# Revit family: R-MBF-271
name_source: partatom
category: Portes
units: mm (PartAtom-declared; Revit-internal decimal feet)

## family parameters
Couper avec des vides une fois chargée = Non
Hôte = Mur
Partagée = Non
Point de calcul de pièce = Oui
Toujours verticalement = Oui

## types (1)
- MBF-271
    1 Vantail = Oui
    2 Vantaux = Non
    A.E.V = non
    Acoustique = non
    Anti-Effraction = non
    Code_MAJ = 2303130305MBF271
    Coloris_Chants = BER
    Coloris_Dormant = Hêtre
    Coloris_Face_Cote_Oppose_Ouverture = Prépeint
    Coloris_Face_Cote_Ouverture = Prépeint
    Construction analytique = <Aucun>
    DAS = Non
    DC Larg Feuillure = 12 mm  [stored 0.0393701 ft]
    DC Pivot Vantail = 60 mm  [stored 0.19685 ft]
    Description = Bloc-porte bois RESISTANT AU FEU 1 vantail grandes dimensions avec pivot linteau encastré et joint anti-pince doigt côté battement, double action / va-et-vient, EI30, sur huisserie bois
    Ep Profil Pose Tunnel = 118 mm
    Ep Strat Vantail = 1 mm  [stored 0.00328084 ft]
    Ep Vantail = 46 mm  [stored 0.150919 ft]
    Epaisseur_Rainure à brique = 8 mm  [stored 0.0262467 ft]
    FDES Inies = https://www.base-inies.fr
https://www.base-inies.fr
    Fabricant = MALERBA
    Fiche_Produit = MBF-271
    Fileur = Non
    Hauteur_Tableau = 2120 mm  [stored 6.95538 ft]
    Hauteur_Vantaux_Souhaitée = 2040 mm  [stored 6.69291 ft]
    Jeu_1 = 0 mm  [stored 0 ft]
    Jeu_2 = 0 mm  [stored 0 ft]
    Jeu_Côté_Articulation_Vantail = 8 mm  [stored 0.0262467 ft]
    Jeu_Côté_Fermeture_Vantail = 8 mm  [stored 0.0262467 ft]
    Jeu_Haut = 3 mm  [stored 0.00984252 ft]
    Larg Profil = 58 mm  [stored 0.190289 ft]
    Larg Profil Avec Fileur = 20 mm  [stored 0.0656168 ft]
    Larg Profil Trav = 76 mm  [stored 0.249344 ft]
    Largeur = 0 mm  [stored 0 ft]
    Largeur_Vantail_Semi_Fixe_Souhaitée = 630 mm  [stored 2.06693 ft]
    Largeur_Vantail_Service_Souhaitée = 930 mm  [stored 3.05118 ft]
    Mat APD = Caoutchouc noir
    Mat Parclose = BER 2
    Mat Parclose Métal = Peinture Laquée PMT - Blanc Pur - RAL 9010
    Materiaux_Dominant = Bois
    Modèle = Va et vient
    Montant_VV = Oui
    Note d'identification = 1V EI30 - GD - LINTEAU (APD MD) - HUISSERIE BOIS
    Profondeur_Rainure à brique = 5 mm  [stored 0.0164042 ft]
    Reference_Commerciale = 1V/DA GD LINTEAU
    Resistance_Feu = EI30
    Sans_Montants = Non
    Sens_Feu = Recto / Verso
    Thermique (W/m2.°K) = 0
    URL = https://www.malerba.fr
    X_Axe Pivot = 114 mm  [stored 0.374016 ft]
    X_DC seuil = 9 mm  [stored 0.0295276 ft]
    X_Inv_DC Larg Feuillure_1V Montant = 12 mm  [stored 0.0393701 ft]

note: [stored X ft] marks values corroborated as IEEE doubles in the binary element streams (Revit-internal decimal feet)

## geometry (parser evidence)
native form markers: Blend x12
no freeform markers — native parametric forms only
